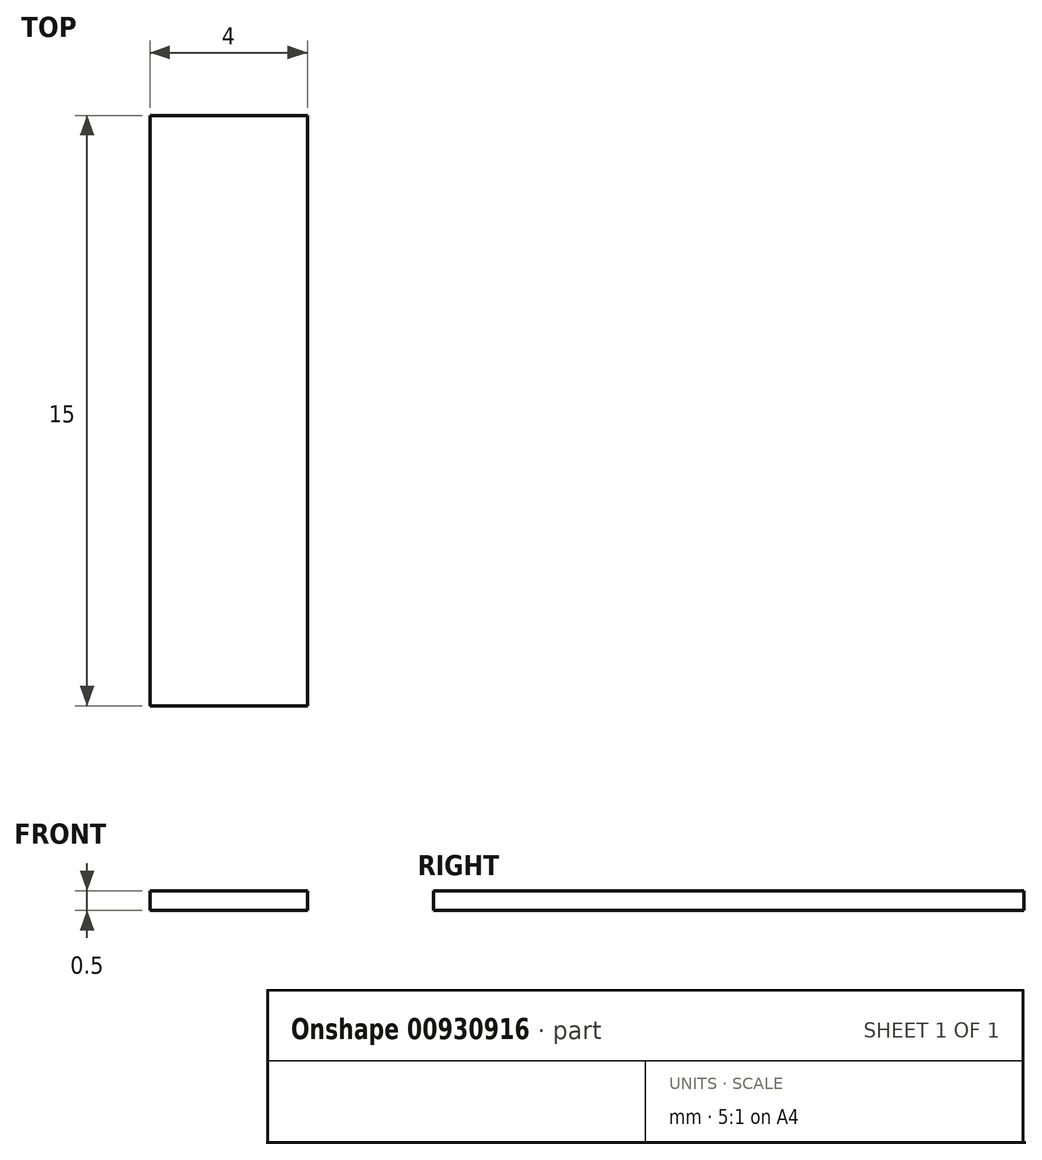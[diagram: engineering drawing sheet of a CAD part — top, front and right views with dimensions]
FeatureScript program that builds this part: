
annotation { "Feature Type Name" : "Feature", "Feature Type Description" : "" }
export const myFeature = defineFeature(function(context is Context, id is Id, definition is map)
    precondition{}
    {
        {
            var Q0;
            Q0=qCreatedBy(makeId("Top.planeOp"),FACE);
            var sketch = newSketch(context, id + "F0", { "sketchPlane" : qUnion([Q0])});
            skLineSegment(sketch, "E0.bottom", {"start": v(2, 7.5) * mm, "end": v(-2, 7.5) * mm});
            skLineSegment(sketch, "E0.top", {"start": v(2, -7.5) * mm, "end": v(-2, -7.5) * mm});
            skLineSegment(sketch, "E0.left", {"start": v(2, 7.5) * mm, "end": v(2, -7.5) * mm});
            skLineSegment(sketch, "E0.right", {"start": v(-2, 7.5) * mm, "end": v(-2, -7.5) * mm});
            skPoint(sketch, "E0.middle", {"position": v(0, 0) * mm});
            skSolve(sketch);
        }
        {
            var Q0;
            Q0=makeQuery(id+"F0.imprint","IMPRINT",FACE,{"disambiguationData":[TD([[makeQuery(id+"F0.imprint","IMPRINT",EDGE,{"derivedFrom":sQuery(id+"F0.wireOp",EDGE,"E0.bottom")}),1.0]])]});
            extrude(context, id + "F1", {"entities" : qUnion([Q0]), "depth" : 0.5 * mm, "offsetDistance" : 25 * mm});
        }
    });
